# Revit family: VTSPEEDW
name_source: partatom
category: Mechanical Equipment
units: mm (PartAtom-declared; Revit-internal decimal feet)

## family parameters
Always vertical = Yes
Classification = None
Cut with Voids When Loaded = No
Maintain Annotation Orientation = No
OmniClass Number = 23.75.70.00
OmniClass Title = HVAC Distribution Devices
Part Type = Normal
Room Calculation Point = No
Round Connector Dimension = Use Diameter
Shared = No
Work Plane-Based = No

## types (1)
- Standard
    Default Elevation = 0' - 0"
    Description = VTSPEEDW
    Design State = 1
    Designer = IM
    Format Version = 0
    Major Version = 5
    Manufacturer = Broan Nutone Venmar
    Minor Version = 0
    Model = VTSPEEDW
    Part Number = VTSPEEDW
    Product Id = PRO/ENGINEER BY PARAMETRIC TECHNOLOGY CORPORATION, 2023424
    Sending System = PRO/ENGINEER BY PARAMETRIC TECHNOLOGY CORPORATION, 2023424

## geometry (parser evidence)
native form markers: Sweep x2
no freeform markers — native parametric forms only
